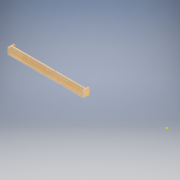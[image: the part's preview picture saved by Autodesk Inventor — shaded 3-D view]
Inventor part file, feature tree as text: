
AUTODESK INVENTOR PART (.ipt)
format: ipt  version: 2022.2 (Build 262287010, 287A)  size: 166,912 bytes
history: native  units: in
note: dims shown in document units (in); Inventor stores cm internally (conversion verified against a paired STEP export)
features: sketch x2, direct_edit x1, extrude x1, projected_geometry x1, revolve x1
ambient origin geometry x8: Origin, YZ Plane, XZ Plane, XY Plane, X Axis, Y Axis, Z Axis, Center Point
bodies: Solid1 (feature_tree), Body1 (feature_tree)
feature tree (6):
  direct_edit  "Direct Edit1"
  sketch  "Sketch1"  dims[d0=180.0deg d1=1.0in d2=0.0in]
  extrude  "Extrusion1"  Depth=1.0in TaperAngle=0.0deg
  sketch  "Sketch2"
  projected_geometry  "Projected Loop1"
  revolve  "Rotate1"  [1 undecoded]
note: 1 required parameter value undecoded (feature->parameter linkage not recoverable at this tier; creation-order binding heuristic only, values carry confidence <= 0.55)
